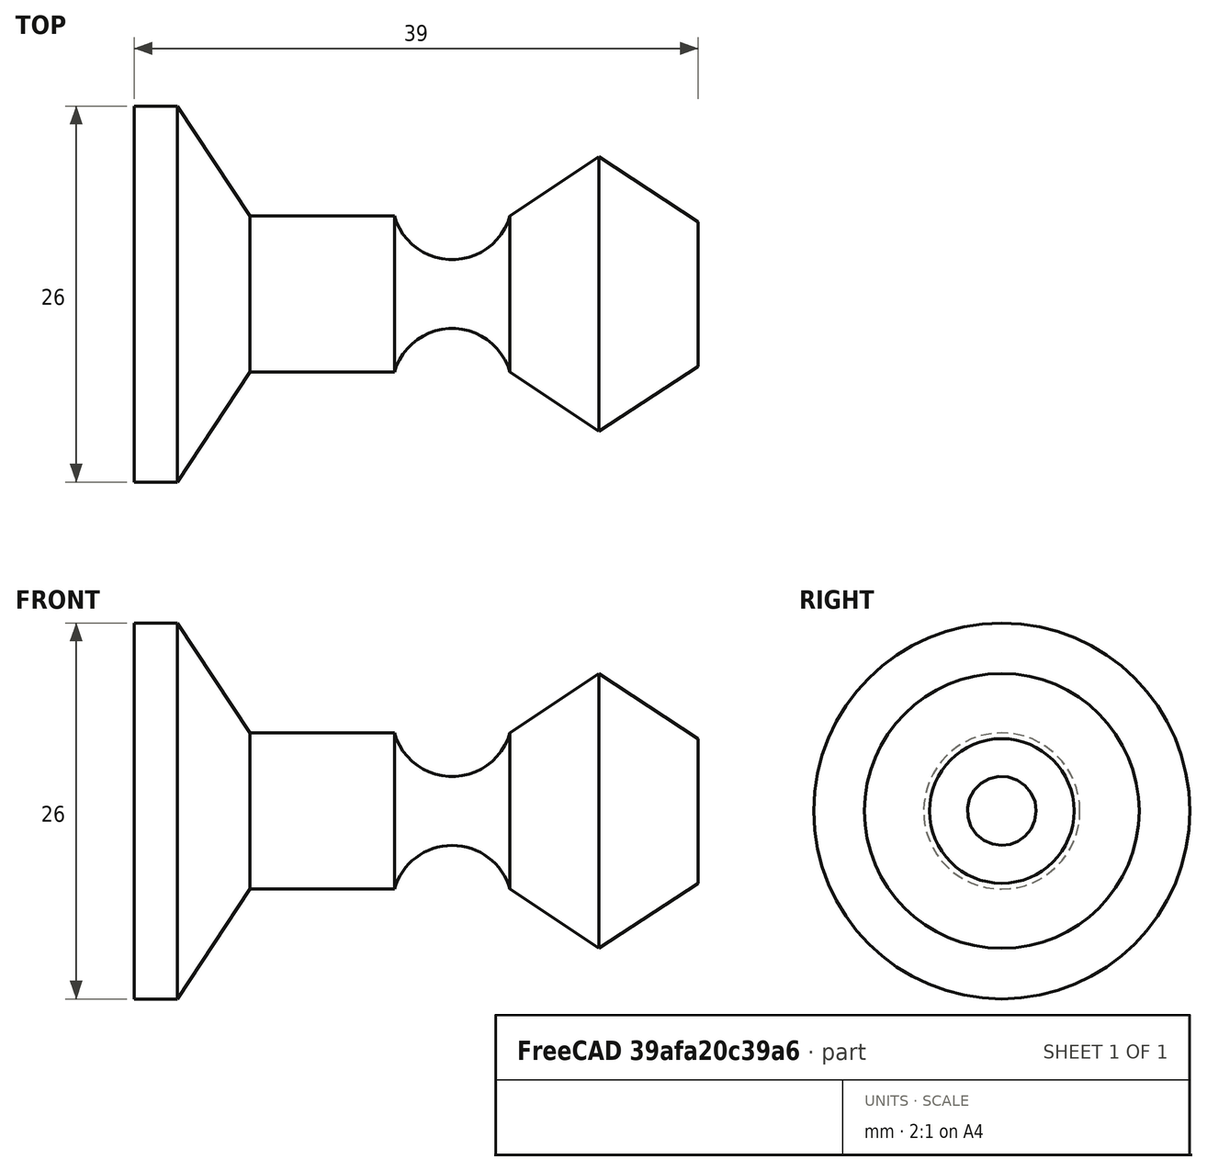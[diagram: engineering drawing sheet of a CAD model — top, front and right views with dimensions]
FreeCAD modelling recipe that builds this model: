
FCSTD DOCUMENT  (FreeCAD 1.0R39109 (Git))
Label: model_test_Segment
License: All rights reserved
LicenseURL: http://en.wikipedia.org/wiki/All_rights_reserved
objects: Part::FeaturePython×13, Part::Part2DObjectPython×12, Part::Feature×6, App::DocumentObjectGroup×4, Sketcher::SketchObject×1, PartDesign::Revolution×1, PartDesign::Body×1
note: 37 computed .brp shape members not serialized (recipe doc carries the construction recipe); baked Part::Feature solids carry a one-line shape summary decoded from their .brp

FEATURE [Sketcher::SketchObject] Sketch
  ArcFitTolerance = 0
  AttachmentSupport = -> [XZ_Plane001]
  FullyConstrained = true
  MakeInternals = false
  MapMode = 5
  Placement = pos=(0,0,0) rot=(1,0,0;1.5708rad)
  sketch-geometry (10):
    g0: LineSegment StartX=-9 StartY=-5 StartZ=0 EndX=-15.85 EndY=-9.5 EndZ=0
    g1: LineSegment StartX=-15.85 StartY=-9.5 StartZ=0 EndX=-22 EndY=-5.4 EndZ=0
    g2: LineSegment StartX=-45 StartY=-13 StartZ=0 EndX=-48 EndY=-13 EndZ=0
    g3: LineSegment StartX=-48 StartY=-13 StartZ=0 EndX=-48 EndY=3.6e-15 EndZ=0
    g4: LineSegment StartX=-48 StartY=4.1e-15 StartZ=0 EndX=10 EndY=4.1e-15 EndZ=0
    g5: ArcOfCircle CenterX=-0.226662 CenterY=0.261315 CenterZ=0 NormalX=0 NormalY=0 NormalZ=1 AngleXU=0 Radius=10.23 StartAngle=3.68179 EndAngle=6.25764
    g6: ArcOfCircle CenterX=-26 CenterY=-6.54263 CenterZ=0 NormalX=0 NormalY=0 NormalZ=1 AngleXU=0 Radius=4.16 StartAngle=0.278247 EndAngle=2.86335
    g7: LineSegment StartX=-30 StartY=-5.4 StartZ=0 EndX=-35 EndY=-5.4 EndZ=0
    g8: LineSegment StartX=-35 StartY=-5.4 StartZ=0 EndX=-40 EndY=-5.4 EndZ=0
    g9: LineSegment StartX=-40 StartY=-5.4 StartZ=0 EndX=-45 EndY=-13 EndZ=0
  constraints (32):
    c: Coincident(g0,g1)
    c: Coincident(g2,g3)
    c: PointOnObject(g3,g-1)
    c: Vertical(g3)
    c: DistanceX(g3) = -48
    c: DistanceY(g3,g3) = 13
    c: DistanceX(g2) = -45
    c: Horizontal(g2)
    c: DistanceX(g0) = -9
    c: DistanceY(g0) = -5
    c: DistanceX(g0) = -15.85
    c: DistanceY(g0) = -9.5
    c: DistanceX(g1) = -22
    c: DistanceY(g1) = -5.4
    c: DistanceX(g6) = -30
    c: Coincident(g4,g3)
    c: Horizontal(g4)
    c: DistanceX(g-1,g4) = 10
    c: Coincident(g5,g4)
    c: Coincident(g5,g0)
    c: Coincident(g6,g1)
    c: Horizontal(g1,g6)
    c: Coincident(g7,g6)
    c: Horizontal(g7)
    c: Coincident(g7,g8)
    c: Horizontal(g8)
    c: Coincident(g8,g9)
    c: Coincident(g9,g2)
    c: DistanceX(g7) = -35
    c: DistanceX(g8) = -40
    c: Radius(g6) = 4.16
    c: Radius(g5) = 10.23
FEATURE [PartDesign::Revolution] Revolution
  Angle = 360
  Angle2 = 60
  Axis = (1,0,0)
  Base = (0,0,0)
  Placement = pos=(0,0,0) rot=(1,0,0;1.5708rad)
  Profile = -> Sketch
  ReferenceAxis = -> X_Axis001
  Reversed = true
  Suppressed = false
  Type = 0
FEATURE [PartDesign::Body] Body001
  AllowCompound = false
  Group = -> [Sketch,Revolution]
  Origin = -> Origin001
  Tip = -> Revolution
FEATURE [Part::Feature] Edge001  label="LineSeg2"
  Placement = pos=(0,0,0) rot=(0.57735,-0.57735,0.57735;2.0944rad)
  shape: bbox 4.1 x 6.888e-07 x 6.15 mm, 0 faces, 0 solids (baked)
FEATURE [Part::Feature] Edge003
  Placement = pos=(0,0,0) rot=(0.57735,-0.57735,0.57735;2.0944rad)
  shape: bbox 2e-07 x 2e-07 x 5 mm, 0 faces, 0 solids (baked)
FEATURE [Part::Feature] Edge004
  Placement = pos=(0,0,0) rot=(0.57735,-0.57735,0.57735;2.0944rad)
  shape: bbox 2e-07 x 2e-07 x 5 mm, 0 faces, 0 solids (baked)
FEATURE [Part::Feature] Edge005
  Placement = pos=(0,0,0) rot=(0.57735,-0.57735,0.57735;2.0944rad)
  shape: bbox 7.6 x 1.106e-06 x 5 mm, 0 faces, 0 solids (baked)
FEATURE [Part::Feature] Edge006
  Placement = pos=(0,0,0) rot=(0.57735,-0.57735,0.57735;2.0944rad)
  shape: bbox 2e-07 x 2e-07 x 3 mm, 0 faces, 0 solids (baked)
FEATURE [Part::Feature] Edge007
  Placement = pos=(0,0,0) rot=(0.57735,-0.57735,0.57735;2.0944rad)
  shape: bbox 13 x 1.75e-06 x 2e-07 mm, 0 faces, 0 solids (baked)
FEATURE [Part::FeaturePython] Point  label="Center1"  # WARN: FeaturePython — macro-defined, semantics opaque (R4)
  Placement = pos=(0,-3.11512e-08,0) rot=(0,0,1;0rad)
  X = 0
  Y = -3.11512e-08
  Z = 0
FEATURE [Part::FeaturePython] Point001  # WARN: FeaturePython — macro-defined, semantics opaque (R4)
  Placement = pos=(3.4e-14,1.066e-13,10) rot=(0,0,1;0rad)
  X = 3.4e-14
  Y = 1.066e-13
  Z = 10
FEATURE [Part::FeaturePython] Point003  # WARN: FeaturePython — macro-defined, semantics opaque (R4)
  Placement = pos=(9.5,1.13249e-06,-15.85) rot=(0,0,1;0rad)
  X = 9.5
  Y = 1.13249e-06
  Z = -15.85
FEATURE [Part::FeaturePython] Point004  # WARN: FeaturePython — macro-defined, semantics opaque (R4)
  Placement = pos=(5.4,6.4373e-07,-22) rot=(0,0,1;0rad)
  X = 5.4
  Y = 6.4373e-07
  Z = -22
FEATURE [Part::FeaturePython] Point005  # WARN: FeaturePython — macro-defined, semantics opaque (R4)
  Placement = pos=(5.4,6.4373e-07,-30) rot=(0,0,1;0rad)
  X = 5.4
  Y = 6.4373e-07
  Z = -30
FEATURE [Part::FeaturePython] Point006  label="Center2"  # WARN: FeaturePython — macro-defined, semantics opaque (R4)
  Placement = pos=(6.54263,7.79942e-07,-26) rot=(0,0,1;0rad)
  X = 6.54263
  Y = 7.79942e-07
  Z = -26
FEATURE [App::DocumentObjectGroup] Group  label="unused"
  Group = -> [Edge003,Edge004,Edge005,Edge006,Edge007]
FEATURE [Part::FeaturePython] Point007  label="Point002"  # WARN: FeaturePython — macro-defined, semantics opaque (R4)
  Placement = pos=(4.85643,-2.62724e-07,-8.74157) rot=(0,0,1;0rad)
  X = 4.85643
  Y = -2.62724e-07
  Z = -8.74157
FEATURE [Part::Part2DObjectPython] Arc001  label="Seg4"  # Draft 2D object (typed FeaturePython)
  Area = 0
  FirstAngle = 15.9424
  LastAngle = 164.058
  MakeFace = true
  Placement = pos=(6.54263,7.79942e-07,-26) rot=(0.57735,-0.57735,0.57735;2.0944rad)
  Radius = 4.16
FEATURE [Part::FeaturePython] Point008  label="Line1Center"  # WARN: FeaturePython — macro-defined, semantics opaque (R4)
  Placement = pos=(7.17821,4.34882e-07,-12.2958) rot=(0,0,1;0rad)
  X = 7.17821
  Y = 4.34882e-07
  Z = -12.2958
FEATURE [Part::FeaturePython] Point009  label="Line2Center"  # WARN: FeaturePython — macro-defined, semantics opaque (R4)
  Placement = pos=(7.45,8.88109e-07,-18.925) rot=(0,0,1;0rad)
  X = 7.45
  Y = 8.88109e-07
  Z = -18.925
FEATURE [Part::Part2DObjectPython] Line  label="LineSeg1"  # Draft 2D object (typed FeaturePython)
  Area = 0
  ChamferSize = 0
  Closed = false
  End = (9.5,1.13249e-06,-15.85)
  FilletRadius = 0
  Length = 8.49073
  MakeFace = true
  Placement = pos=(4.85643,-2.62724e-07,-8.74157) rot=(0.57735,-0.57735,0.57735;2.0944rad)
  Points = (2) [(0,0,0),(-7.10843,-4.64357,-1.54213e-06)]
  Start = (4.85643,-2.62724e-07,-8.74157)
  Subdivisions = 0
FEATURE [Part::Part2DObjectPython] Arc  label="ArcSeg1"  # Draft 2D object (typed FeaturePython)
  Area = 0
  FirstAngle = -150.945
  LastAngle = -1.02453e-05
  MakeFace = true
  Placement = pos=(0,-3.11512e-08,0) rot=(0.57735,-0.57735,0.57735;2.0944rad)
  Radius = 10
FEATURE [Part::Part2DObjectPython] Line001  # Draft 2D object (typed FeaturePython)
  Area = 0
  ChamferSize = 0
  Closed = false
  End = (4.85643,-2.62724e-07,-8.74157)
  FilletRadius = 0
  Length = 19.3606
  MakeFace = true
  Placement = pos=(-1.04e-13,5.64895e-07,10) rot=(0.57735,-0.57735,0.57735;2.0944rad)
  Points = (2) [(0,0,0),(-18.7416,-4.85643,1.97994e-20)]
  Start = (-1.041e-13,5.64895e-07,10)
  Subdivisions = 0
FEATURE [Part::Part2DObjectPython] Line005  label="LineSeg1Intersect"  # Draft 2D object (typed FeaturePython)
  Area = 0
  ChamferSize = 0
  Closed = false
  End = (10.7324,7.00265e-07,-9.974)
  FilletRadius = 0
  Length = 8.49073
  MakeFace = true
  Placement = pos=(3.624,1.69499e-07,-14.6176) rot=(0,-0.707107,0.707107;3.14159rad)
  Points = (2) [(0,0,0),(-7.10843,-4.64357,-1.54213e-06)]
  Start = (3.624,1.69499e-07,-14.6176)
  Subdivisions = 0
FEATURE [Part::FeaturePython] Point010  label="IntersectExtend"  # WARN: FeaturePython — macro-defined, semantics opaque (R4)
  Placement = pos=(15.4887,-3.02654e-06,-6.86699) rot=(0,0,1;0rad)
  X = 15.4887
  Y = -3.02654e-06
  Z = -6.86699
FEATURE [Part::Part2DObjectPython] Line006  label="ArcSeg2Intersect"  # Draft 2D object (typed FeaturePython)
  Area = 0
  ChamferSize = 0
  Closed = false
  End = (4.4,4.73417e-07,-30)
  FilletRadius = 0
  Length = 8
  MakeFace = true
  Placement = pos=(5.4,6.4373e-07,-22) rot=(0.57735,-0.57735,0.57735;2.0944rad)
  Points = (2) [(3.55271e-15,1,2.08616e-07),(-8,1,6.17347e-07)]
  Start = (4.4,6.4373e-07,-22)
  Subdivisions = 0
FEATURE [Part::Part2DObjectPython] Line007  label="ArcSeg1Intersect"  # Draft 2D object (typed FeaturePython)
  Area = 0
  ChamferSize = 0
  Closed = false
  End = (12,-1.93508e-06,0)
  FilletRadius = 0
  Length = 7
  MakeFace = true
  Placement = pos=(2.42821,1.51086e-07,0.629214) rot=(0.57735,-0.57735,0.57735;2.0944rad)
  Points = (2) [(-0.629214,-2.57179,-5.17764e-07),(-0.629214,-9.57179,1.08085e-07)]
  Start = (5,1.51086e-07,0)
  Subdivisions = 0
FEATURE [Part::Part2DObjectPython] Line008  label="apothem001"  # Draft 2D object (typed FeaturePython)
  Area = 0
  ChamferSize = 0
  Closed = false
  End = (2.42821,1.51086e-07,0.629214)
  FilletRadius = 0
  Length = 2.50841
  MakeFace = true
  Placement = pos=(0,-3.11512e-08,0) rot=(0.57735,-0.57735,0.57735;2.0944rad)
  Points = (2) [(0,0,0),(0.629213,-2.42821,1.16136e-20)]
  Start = (0,0,0)
  Subdivisions = 0
FEATURE [Part::Part2DObjectPython] Arc003  label="largeArcSeg"  # Draft 2D object (typed FeaturePython)
  Area = 0
  FirstAngle = -90
  LastAngle = 119.055
  MakeFace = true
  Placement = pos=(4.85643,3.33323e-07,1.25843) rot=(1,0,0;1.5708rad)
  Radius = 10
FEATURE [Part::FeaturePython] Point011  label="largeArgCenter"  # WARN: FeaturePython — macro-defined, semantics opaque (R4)
  Placement = pos=(4.85643,3.33323e-07,1.25843) rot=(0,0,1;0rad)
  X = 4.85643
  Y = 3.33323e-07
  Z = 1.25843
FEATURE [Part::Part2DObjectPython] Line009  # Draft 2D object (typed FeaturePython)
  Area = 0
  ChamferSize = 0
  Closed = false
  End = (7.07107,-3.11512e-08,2.92893)
  FilletRadius = 0
  Length = 10
  MakeFace = true
  Placement = pos=(-8.88e-14,3.33323e-07,10) rot=(0.862856,-0.357407,0.357407;1.71777rad)
  Points = (2) [(0,0,0),(8.82055e-14,-10,3.64474e-07)]
  Start = (-8.88e-14,3.33323e-07,10)
  Subdivisions = 0
FEATURE [Part::Part2DObjectPython] Line010  # Draft 2D object (typed FeaturePython)
  Area = 0
  ChamferSize = 0
  Closed = false
  End = (1.76777,1.51086e-07,4.6967)
  FilletRadius = 0
  Length = 2.5
  MakeFace = true
  Placement = pos=(3.53553,1.51086e-07,6.46447) rot=(1,0,0;1.5708rad)
  Points = (2) [(0,0,0),(-1.76777,-1.76777,-2.39442e-16)]
  Start = (3.53553,1.51086e-07,6.46447)
  Subdivisions = 0
FEATURE [App::DocumentObjectGroup] Group003  label="helper"
  Group = -> [Line001,Line008,Line009,Line010]
FEATURE [Part::Part2DObjectPython] Arc004  label="partialArc"  # Draft 2D object (typed FeaturePython)
  Area = 0
  FirstAngle = -18.4349
  LastAngle = 108.435
  MakeFace = true
  Placement = pos=(1.76777,1.51086e-07,4.6967) rot=(1,0,0;1.5708rad)
  Radius = 5.59017
FEATURE [App::DocumentObjectGroup] Group002  label="Segments"
  Group = -> [Arc,Line005,Arc001,Edge001,Line006,Line007,Line,Arc003,Arc004]
FEATURE [Part::FeaturePython] Point012  label="partialArcCenter"  # WARN: FeaturePython — macro-defined, semantics opaque (R4)
  Placement = pos=(1.76777,1.51086e-07,4.6967) rot=(0,0,1;0rad)
  X = 1.76777
  Y = 1.51086e-07
  Z = 4.6967
FEATURE [App::DocumentObjectGroup] Group001  label="Points"
  Group = -> [Point,Point007,Point003,Point004,Point005,Point006,Point001,Point012,Point010,Point011]
FEATURE [Part::FeaturePython] Point013  # WARN: FeaturePython — macro-defined, semantics opaque (R4)
  Placement = pos=(3,0,-7.5) rot=(0,0,1;0rad)
  X = 3
  Y = 0
  Z = -7.5
